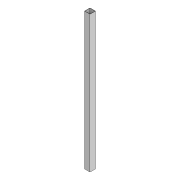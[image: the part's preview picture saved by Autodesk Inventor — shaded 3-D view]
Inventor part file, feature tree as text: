
AUTODESK INVENTOR PART (.ipt)
format: ipt  version: 2022 (Build 260153000, 153)  size: 79,872 bytes
history: native  units: mm
features: extrude x1, sketch x1
ambient origin geometry x8: Origin, YZ Plane, XZ Plane, XY Plane, X Axis, Y Axis, Z Axis, Center Point
bodies: Solid1 (feature_tree)
feature tree (2):
  extrude  "Extrusion1"  Depth=20.0mm
  sketch  "Sketch1"  dims[d0=20.0mm d1=20.0mm d2=1.0mm d3=500.0mm d4=0.0mm]
